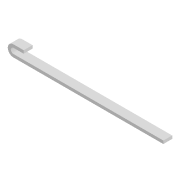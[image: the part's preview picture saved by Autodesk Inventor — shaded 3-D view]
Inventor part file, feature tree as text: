
AUTODESK INVENTOR PART (.ipt)
format: ipt  version: 2020 (Build 240168000, 168)  size: 85,504 bytes
history: native  units: mm
features: extrude x1, sketch x1
ambient origin geometry x8: Origin, YZ Plane, XZ Plane, XY Plane, X Axis, Y Axis, Z Axis, Center Point
bodies: Solid1 (feature_tree)
feature tree (2):
  extrude  "Extrusion1"  Depth=20.0mm
  sketch  "Sketch1"  dims[d0=76.0mm d1=20.0mm d2=20.0mm d4=1000.0mm d5=59.0mm d6=0.0mm d7=68.0mm]
